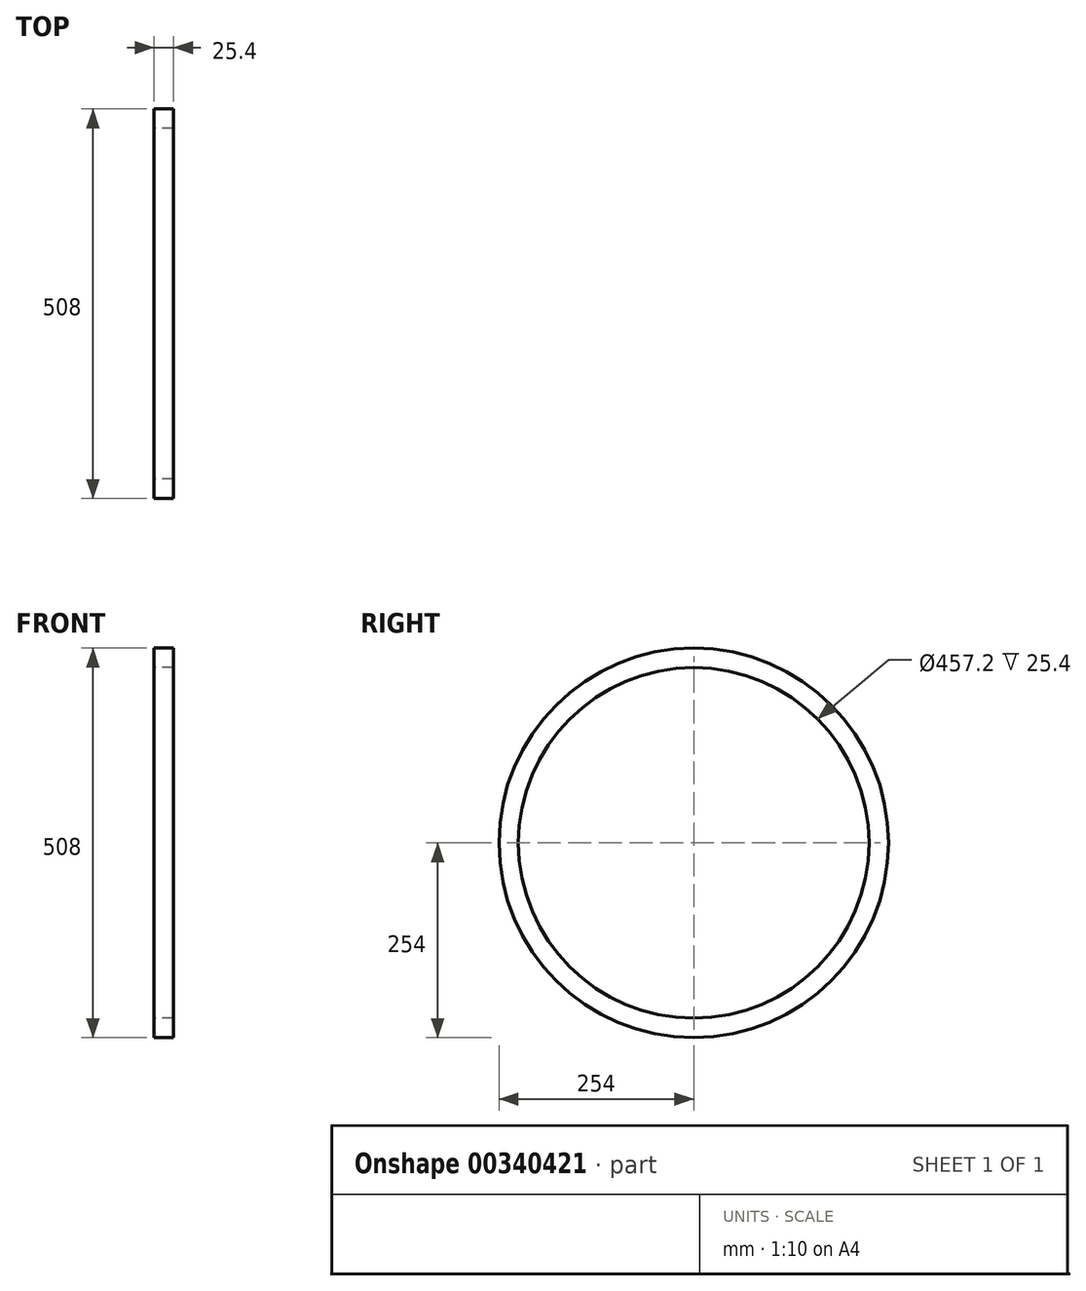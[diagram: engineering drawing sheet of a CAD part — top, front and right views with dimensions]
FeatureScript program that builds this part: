
annotation { "Feature Type Name" : "Feature", "Feature Type Description" : "" }
export const myFeature = defineFeature(function(context is Context, id is Id, definition is map)
    precondition{}
    {
        {
            var Q0;
            Q0=qCreatedBy(makeId("Right.planeOp"),FACE);
            var sketch = newSketch(context, id + "F0", { "sketchPlane" : qUnion([Q0])});
            skCircle(sketch, "E0", {"center": v(0, 0) * mm, "radius": 254 * mm});
            skCircle(sketch, "E1", {"center": v(0, 0) * mm, "radius": 228.6 * mm});
            skSolve(sketch);
        }
        {
            var Q0;
            Q0=makeQuery(id+"F0.imprint","IMPRINT",FACE,{"disambiguationData":[TD([[makeQuery(id+"F0.imprint","IMPRINT",EDGE,{"derivedFrom":sQuery(id+"F0.wireOp",EDGE,"E0")}),1.0]])]});
            extrude(context, id + "F1", {"entities" : qUnion([Q0]), "depth" : 25.4 * mm, "offsetDistance" : 25.4 * mm});
        }
    });
